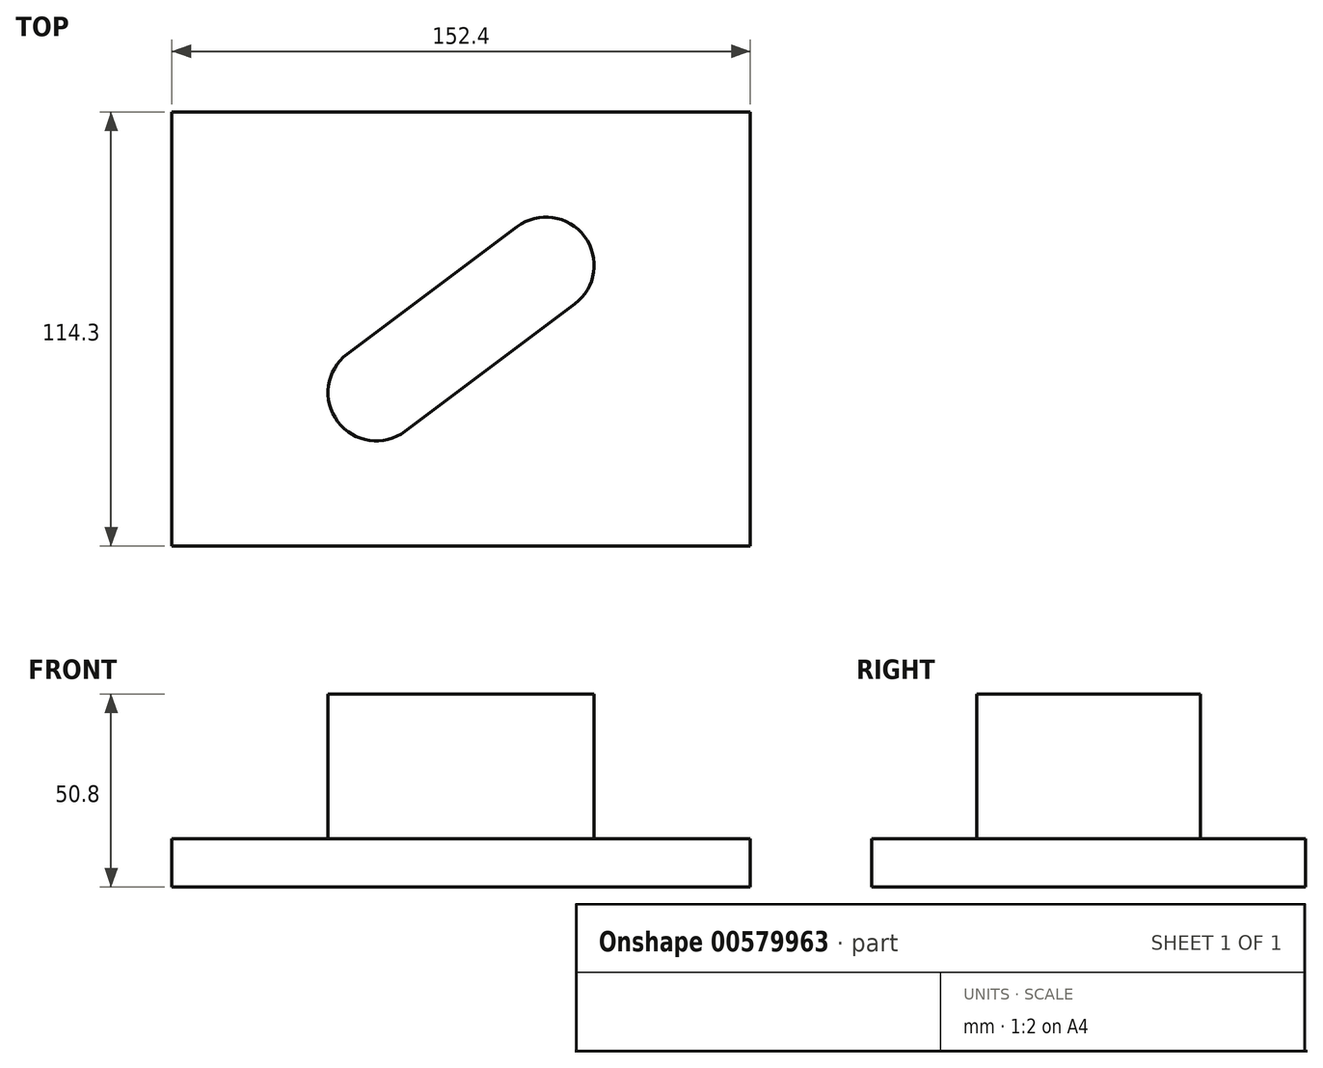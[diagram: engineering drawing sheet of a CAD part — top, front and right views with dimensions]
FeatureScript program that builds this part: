
annotation { "Feature Type Name" : "Feature", "Feature Type Description" : "" }
export const myFeature = defineFeature(function(context is Context, id is Id, definition is map)
    precondition{}
    {
        {
            var Q0;
            Q0=qCreatedBy(makeId("Top.planeOp"),FACE);
            var sketch = newSketch(context, id + "F0", { "sketchPlane" : qUnion([Q0])});
            skLineSegment(sketch, "E0", {"start": v(0, 0) * mm, "end": v(152.4, 0) * mm});
            skLineSegment(sketch, "E1", {"start": v(152.4, 0) * mm, "end": v(152.4, -114.3) * mm});
            skLineSegment(sketch, "E2", {"start": v(152.4, -114.3) * mm, "end": v(0, -114.3) * mm});
            skLineSegment(sketch, "E3", {"start": v(0, -114.3) * mm, "end": v(0, 0) * mm});
            skSolve(sketch);
        }
        {
            var Q0;
            Q0=makeQuery(id+"F0.imprint","IMPRINT",FACE,{"disambiguationData":[TD([[makeQuery(id+"F0.imprint","IMPRINT",EDGE,{"derivedFrom":sQuery(id+"F0.wireOp",EDGE,"E0")}),-1.0]])]});
            extrude(context, id + "F1", {"entities" : qUnion([Q0]), "depth" : 12.7 * mm, "offsetDistance" : 25.4 * mm});
        }
        {
            var Q0;
            Q0=makeQuery(id+"F1.opExtrude","CAP_FACE",FACE,{"disambiguationData":[OSD([sQuery(id+"F0.wireOp",EDGE,"E0"),sQuery(id+"F0.wireOp",EDGE,"E1"),sQuery(id+"F0.wireOp",EDGE,"E2"),sQuery(id+"F0.wireOp",EDGE,"E3")])],"isStart":false});
            var sketch = newSketch(context, id + "F2", { "sketchPlane" : qUnion([Q0])});
            skLineSegment(sketch, "E4", {"start": v(0, -57.15) * mm, "end": v(152.4, -57.15) * mm});
            skLineSegment(sketch, "E5", {"start": v(76.2, 0) * mm, "end": v(76.2, -114.3) * mm});
            skLineSegment(sketch, "E6", {"start": v(76.2, -57.15) * mm, "end": v(152.4, 0) * mm});
            skLineSegment(sketch, "E7", {"start": v(76.2, -57.15) * mm, "end": v(0, -114.3) * mm});
            skLineSegment(sketch, "E8", {"start": v(76.2, -57.15) * mm, "end": v(98.55, -40.39) * mm});
            skLineSegment(sketch, "E9", {"start": v(76.2, -57.15) * mm, "end": v(53.85, -73.91) * mm});
            skLineSegment(sketch, "E10", {"start": v(53.85, -73.91) * mm, "end": v(61.47, -84.07) * mm});
            skLineSegment(sketch, "E11", {"start": v(53.85, -73.91) * mm, "end": v(46.23, -63.75) * mm});
            skLineSegment(sketch, "E12", {"start": v(98.55, -40.39) * mm, "end": v(106.17, -50.55) * mm});
            skLineSegment(sketch, "E13", {"start": v(98.55, -40.39) * mm, "end": v(90.93, -30.23) * mm});
            skLineSegment(sketch, "E14", {"start": v(90.93, -30.23) * mm, "end": v(46.23, -63.75) * mm});
            skLineSegment(sketch, "E15", {"start": v(61.47, -84.07) * mm, "end": v(106.17, -50.55) * mm});
            skCircle(sketch, "E16", {"center": v(98.55, -40.39) * mm, "radius": 12.7 * mm});
            skCircle(sketch, "E17", {"center": v(53.85, -73.91) * mm, "radius": 12.7 * mm});
            skSolve(sketch);
        }
        {
            var Q0;
            Q0 = qSketchRegion(id + "F2", true);
            extrude(context, id + "F3", {"entities" : qUnion([Q0]), "operationType" : NewBodyOperationType.ADD, "depth" : 38.1 * mm, "offsetDistance" : 25.4 * mm});
        }
    });
